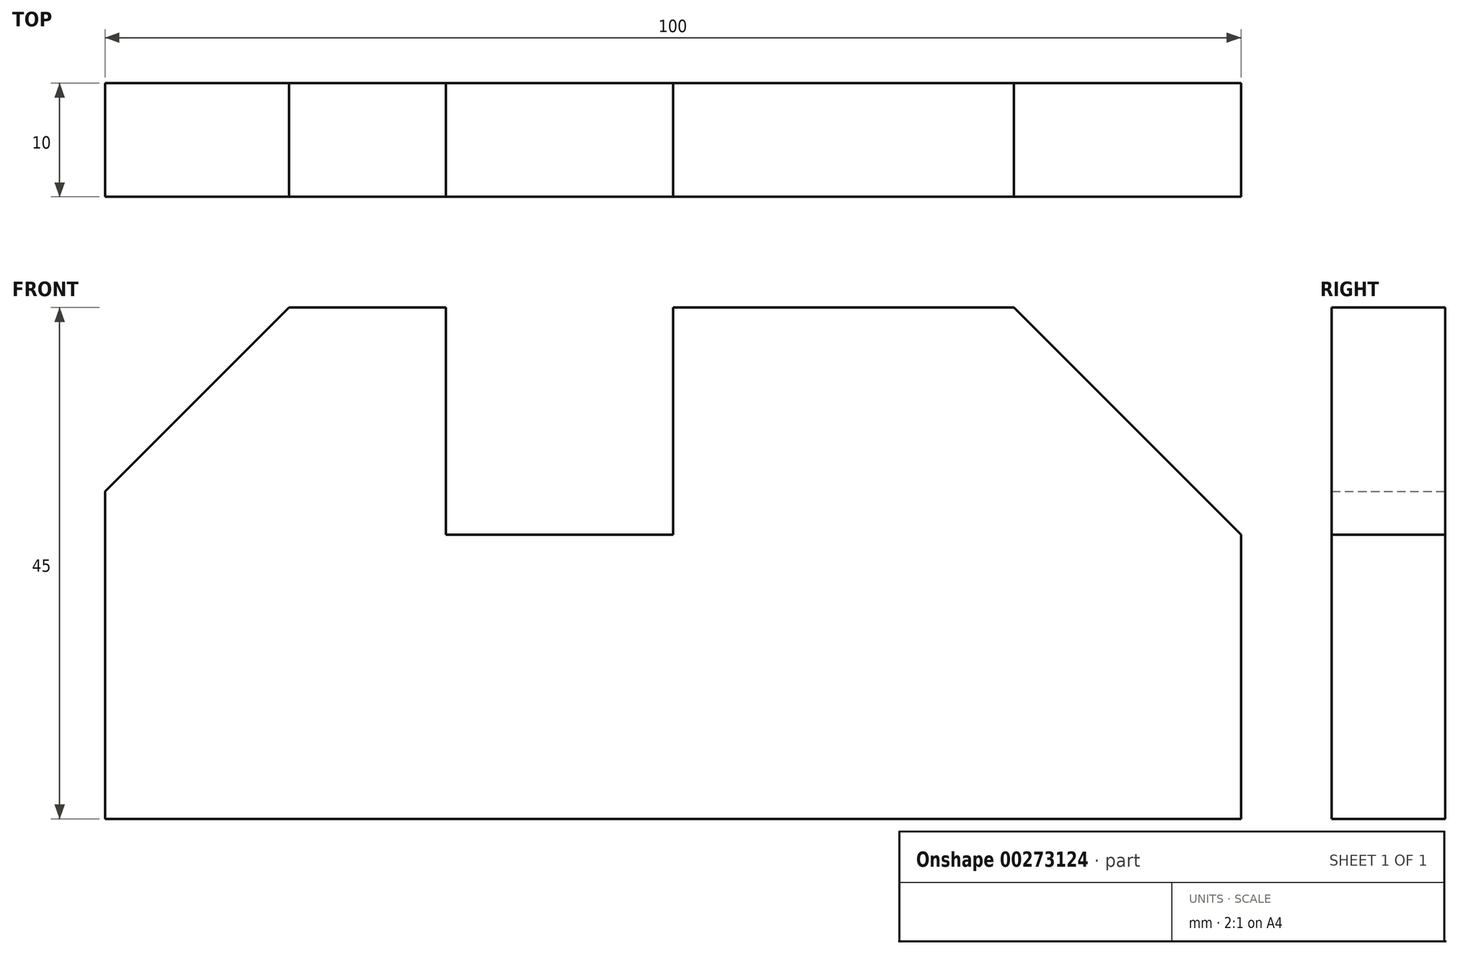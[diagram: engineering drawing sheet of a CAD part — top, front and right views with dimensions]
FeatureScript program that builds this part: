
annotation { "Feature Type Name" : "Feature", "Feature Type Description" : "" }
export const myFeature = defineFeature(function(context is Context, id is Id, definition is map)
    precondition{}
    {
        {
            var Q0;
            Q0=qCreatedBy(makeId("Front.planeOp"),FACE);
            var sketch = newSketch(context, id + "F0", { "sketchPlane" : qUnion([Q0])});
            skLineSegment(sketch, "E0", {"start": v(0, 0) * mm, "end": v(100, 0) * mm});
            skLineSegment(sketch, "E1", {"start": v(100, 0) * mm, "end": v(100, 25) * mm});
            skLineSegment(sketch, "E2", {"start": v(100, 25) * mm, "end": v(80, 45) * mm});
            skLineSegment(sketch, "E3", {"start": v(80, 45) * mm, "end": v(50, 45) * mm});
            skLineSegment(sketch, "E4", {"start": v(50, 45) * mm, "end": v(50, 25) * mm});
            skLineSegment(sketch, "E5", {"start": v(50, 25) * mm, "end": v(30, 25) * mm});
            skLineSegment(sketch, "E6", {"start": v(30, 25) * mm, "end": v(30, 45) * mm});
            skLineSegment(sketch, "E7", {"start": v(30, 45) * mm, "end": v(16.2, 45) * mm});
            skLineSegment(sketch, "E8", {"start": v(16.2, 45) * mm, "end": v(0, 28.8) * mm});
            skLineSegment(sketch, "E9", {"start": v(0, 28.8) * mm, "end": v(0, 0) * mm});
            skSolve(sketch);
        }
        {
            var Q0;
            Q0=makeQuery(id+"F0.imprint","IMPRINT",FACE,{"disambiguationData":[TD([[makeQuery(id+"F0.imprint","IMPRINT",EDGE,{"derivedFrom":sQuery(id+"F0.wireOp",EDGE,"E0")}),1.0]])]});
            extrude(context, id + "F1", {"entities" : qUnion([Q0]), "depth" : 10 * mm});
        }
    });
